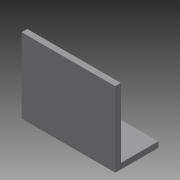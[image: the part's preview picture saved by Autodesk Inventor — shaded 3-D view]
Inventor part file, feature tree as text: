
AUTODESK INVENTOR PART (.ipt)
format: ipt  version: 2013 SP2 (Build 170200200, 200)  size: 77,824 bytes
history: native  units: mm
features: extrude x2, sketch x2
ambient origin geometry x8: Origin, YZ Plane, XZ Plane, XY Plane, X Axis, Y Axis, Z Axis, Center Point
bodies: Solid1 (feature_tree)
feature tree (4):
  extrude  "Extrusion1"  Depth=20.0mm
  extrude  "Extrusion2"  Depth=40.0mm
  sketch  "Sketch1"  dims[d0=50.0mm d1=20.0mm]
  sketch  "Sketch2"  dims[d2=3.0mm d3=0.0mm d4=40.0mm d5=3.0mm d6=0.0mm]
